# Revit family: KEUCO_14982010037
name_source: partatom
category: Möbel
revit_build: Autodesk Revit 2016 (Build: 20150220_1215(x64)
units: mm (PartAtom-declared; Revit-internal decimal feet)

## family parameters
Arbeitsebenenbasiert = Nein
Beim Laden mit Abzugskörper schneiden = Nein
Gemeinsam genutzt = Nein
Immer vertikal = Ja
Raumberechnungspunkt = Nein

## types (6) — shared parameters
Beschreibung = auch für den Naßbereich geeignet
Gewicht = 0.628
Hersteller = KEUCO
Kategorie = ACC
Preisgruppe = 1
Serie = Plan
URL = https://www.keuco.com
Verwendung = DU / WA / WP

## per-type parameters (varying)
| type | Ausschreibungstext | Material Beine | Material Sitz |
| 14982010037 | KEUCO PLAN Hocker 14982010037 
mit zwei hochglanzverchromten, rutschsicheren Fußelementen, 
auch für den Naßbereich geeignet
hochglanzverchromtes zylindrisches Griffstück, 
Sitzfläche aus Polypropylen schwarzgrau (RAL 7021),
340 mm x 365 mm, Sitzhöhe 469 mm
Belastbarkeit 100 kg | Verchromt | Schwarzgrau (RAL 7021) |
| 14982010038 | KEUCO PLAN Hocker 14982010038 
mit zwei hochglanzverchromten, rutschsicheren Fußelementen, 
auch für den Naßbereich geeignet
hochglanzverchromtes zylindrisches Griffstück, 
Sitzfläche aus Polypropylen lichtgrau (RAL 7035),
340 mm x 365 mm, Sitzhöhe 469 mm
Belastbarkeit 100 kg | Verchromt | Lichtgrau (RAL 7035) |
| 14982010051 | KEUCO PLAN Hocker 14982010051 
mit zwei hochglanzverchromten, rutschsicheren Fußelementen, 
auch für den Naßbereicht geeignet
hochglanzverchromtes zylindrisches Griffstück, 
Sitzfläche aus Polypropylen weiß (RAL 9010) ,
340 mm x 365 mm, Sitzhöhe 469 mm
Belastbarkeit 100 kg | Verchromt | Weiß (RAL 9010) |
| 14982170037 | KEUCO PLAN Hocker 14982170037 
mit zwei Aluminium lackierten, rutschsicheren Fußelementen, 
auch für den Naßbereicht geeignet
hochglanzverchromtes zylindrisches Griffstück, 
Sitzfläche aus Polypropylen schwarzgrau (RAL 7021),
340 mm x 365 mm, Sitzhöhe 469 mm
Belastbarkeit 100 kg | Aluminium silber-eloxiert (E6 EV1) | Schwarzgrau (RAL 7021) |
| 14982170038 | KEUCO PLAN Hocker 14982170038
mit zwei Aluminium lackierten, rutschsicheren Fußelementen, 
auch für den Naßbereicht geeignet
hochglanzverchromtes zylindrisches Griffstück, 
Sitzfläche aus Polypropylen lichtgrau (RAL 7021),
340 mm x 365 mm, Sitzhöhe 469 mm
Belastbarkeit 100 kg | Aluminium silber-eloxiert (E6 EV1) | Lichtgrau (RAL 7035) |
| 14982170051 | KEUCO PLAN Hocker 14982170051
mit zwei Aluminium lackierten, rutschsicheren Fußelementen, 
auch für den Naßbereicht geeignet
hochglanzverchromtes zylindrisches Griffstück, 
Sitzfläche aus Polypropylen weiß (RAL 9010),
340 mm x 365 mm, Sitzhöhe 469 mm
Belastbarkeit 100 kg | Aluminium silber-eloxiert (E6 EV1) | Schwarzgrau (RAL 7021) |

note: column(s) folded — value = type name in every type: Artikelnummer

## geometry (parser evidence)
native form markers: Sweep x3
no freeform markers — native parametric forms only
